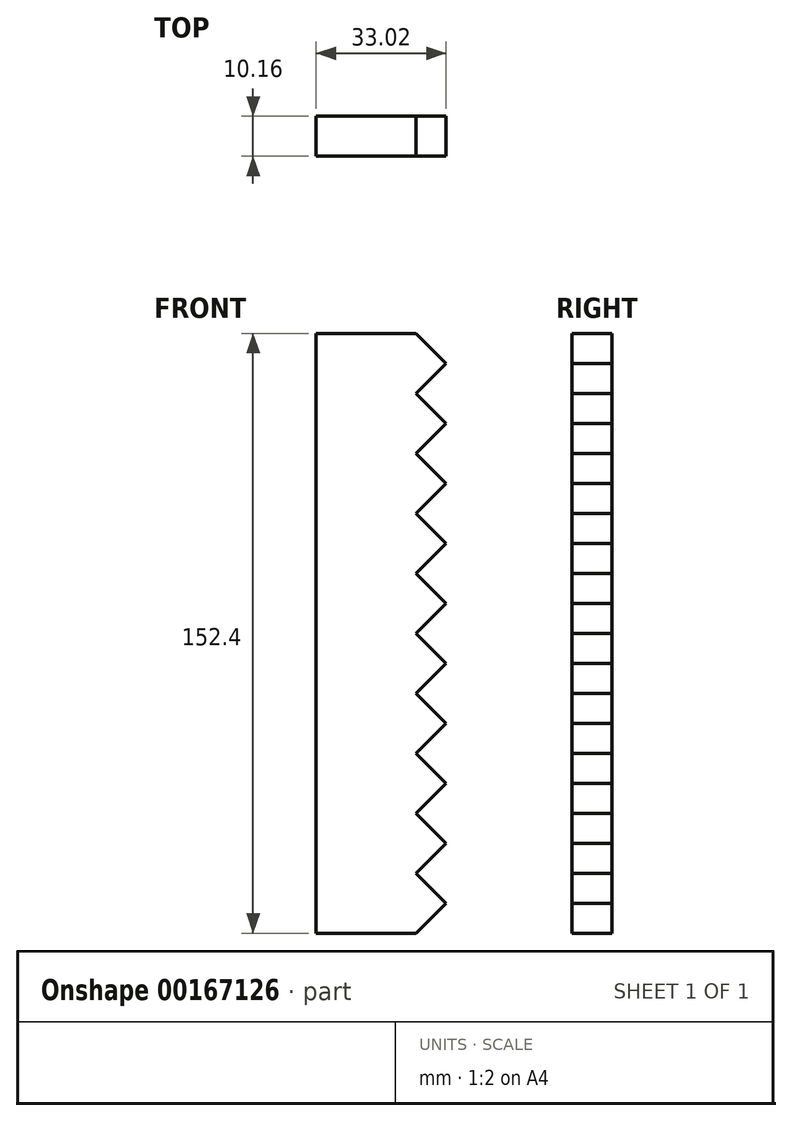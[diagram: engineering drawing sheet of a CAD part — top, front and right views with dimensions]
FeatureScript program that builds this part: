
annotation { "Feature Type Name" : "Feature", "Feature Type Description" : "" }
export const myFeature = defineFeature(function(context is Context, id is Id, definition is map)
    precondition{}
    {
        {
            var Q0;
            Q0=qCreatedBy(makeId("Front.planeOp"),FACE);
            var sketch = newSketch(context, id + "F0", { "sketchPlane" : qUnion([Q0])});
            skLineSegment(sketch, "E0.bottom", {"start": v(-46.07, 77.99) * mm, "end": v(-20.67, 77.99) * mm});
            skLineSegment(sketch, "E0.top", {"start": v(-46.07, -74.41) * mm, "end": v(-20.67, -74.41) * mm});
            skLineSegment(sketch, "E0.left", {"start": v(-46.07, 77.99) * mm, "end": v(-46.07, -74.41) * mm});
            skLineSegment(sketch, "E1", {"start": v(-20.67, 77.99) * mm, "end": v(-13.05, 70.37) * mm});
            skLineSegment(sketch, "E2", {"start": v(-13.05, 70.37) * mm, "end": v(-20.67, 62.75) * mm});
            skLineSegment(sketch, "E3", {"start": v(-20.67, 62.75) * mm, "end": v(-13.05, 55.13) * mm});
            skLineSegment(sketch, "E4", {"start": v(-13.05, 55.13) * mm, "end": v(-20.67, 47.5) * mm});
            skLineSegment(sketch, "E5", {"start": v(-20.67, 47.5) * mm, "end": v(-13.05, 39.89) * mm});
            skLineSegment(sketch, "E6", {"start": v(-13.05, 39.89) * mm, "end": v(-20.67, 32.27) * mm});
            skLineSegment(sketch, "E7", {"start": v(-20.67, 32.27) * mm, "end": v(-13.05, 24.65) * mm});
            skLineSegment(sketch, "E8", {"start": v(-13.05, 24.65) * mm, "end": v(-20.67, 17.03) * mm});
            skLineSegment(sketch, "E9", {"start": v(-20.67, 17.03) * mm, "end": v(-13.05, 9.4) * mm});
            skLineSegment(sketch, "E10", {"start": v(-13.05, 9.4) * mm, "end": v(-20.67, 1.79) * mm});
            skLineSegment(sketch, "E11", {"start": v(-20.67, 1.79) * mm, "end": v(-13.05, -5.83) * mm});
            skLineSegment(sketch, "E12", {"start": v(-13.05, -5.83) * mm, "end": v(-20.67, -13.45) * mm});
            skLineSegment(sketch, "E13", {"start": v(-20.67, -13.45) * mm, "end": v(-13.05, -21.07) * mm});
            skLineSegment(sketch, "E14", {"start": v(-13.05, -21.07) * mm, "end": v(-20.67, -28.7) * mm});
            skLineSegment(sketch, "E15", {"start": v(-20.67, -28.7) * mm, "end": v(-13.05, -36.31) * mm});
            skLineSegment(sketch, "E16", {"start": v(-13.05, -36.31) * mm, "end": v(-20.67, -43.93) * mm});
            skLineSegment(sketch, "E17", {"start": v(-20.67, -43.93) * mm, "end": v(-13.05, -51.55) * mm});
            skLineSegment(sketch, "E18", {"start": v(-13.05, -51.55) * mm, "end": v(-20.67, -59.17) * mm});
            skLineSegment(sketch, "E19", {"start": v(-20.67, -59.17) * mm, "end": v(-13.05, -66.8) * mm});
            skLineSegment(sketch, "E20", {"start": v(-13.05, -66.8) * mm, "end": v(-20.67, -74.41) * mm});
            skSolve(sketch);
        }
        {
            var Q0;
            Q0=makeQuery(id+"F0.imprint","IMPRINT",FACE,{"disambiguationData":[TD([[makeQuery(id+"F0.imprint","IMPRINT",EDGE,{"derivedFrom":sQuery(id+"F0.wireOp",EDGE,"E0.bottom")}),-1.0]])]});
            extrude(context, id + "F1", {"entities" : qUnion([Q0]), "endBound" : BoundingType.SYMMETRIC, "depth" : 10.16 * mm});
        }
    });
